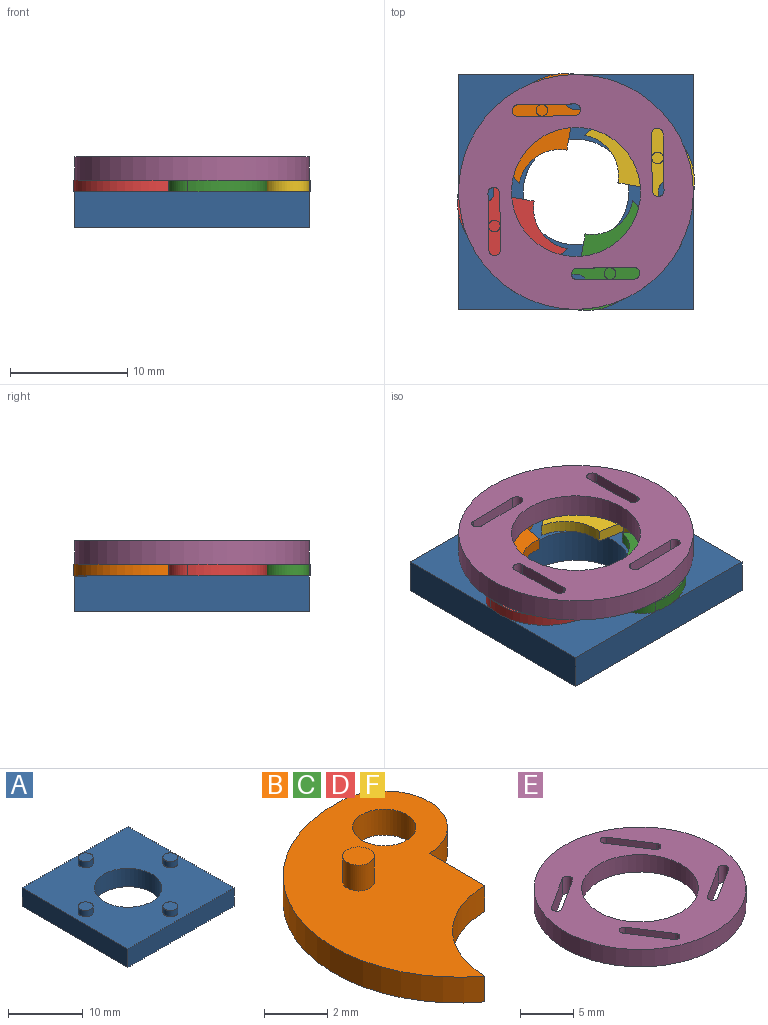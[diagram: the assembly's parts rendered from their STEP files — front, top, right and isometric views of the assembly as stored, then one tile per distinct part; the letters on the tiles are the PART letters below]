
ASSEMBLY  parts=6 mates=6
PART A: 15 faces, bbox 20x20x4 mm
  f0: plane 20x3mm, normal (1,0,0), area 60mm2, adj f1,f4,f5,f6
  f1: plane 20x3mm, normal (0,1,0), area 60mm2, adj f0,f2,f5,f6
  f2: plane 20x3mm, normal (-1,0,0), area 60mm2, adj f1,f4,f5,f6
  f3: cylinder r=4.5mm len=9mm, axis (0,0,-1), area 84.8mm2, adj f5,f6
  f4: plane 20x3mm, normal (0,-1,0), area 60mm2, adj f0,f2,f5,f6
  f5: plane 20x20mm, normal (0,0,1), area 323.8mm2, adj f0,f1,f2,f3,f4,f7,f9,f11
  f6: plane 20x20mm, normal (0,0,-1), area 336.4mm2, adj f0,f1,f2,f3,f4
  f7: cylinder r=1mm len=2mm, axis (0,0,-1), area 6.3mm2, adj f5,f8
  f8: plane 2x2mm, normal (0,0,1), area 3.1mm2, adj f7
  f9: cylinder r=1mm len=2mm, axis (0,0,-1), area 6.3mm2, adj f5,f10
  f10: plane 2x2mm, normal (0,0,1), area 3.1mm2, adj f9
  f11: cylinder r=1mm len=2mm, axis (0,0,-1), area 6.3mm2, adj f5,f12
  f12: plane 2x2mm, normal (0,0,1), area 3.1mm2, adj f11
  f13: cylinder r=1mm len=2mm, axis (0,0,-1), area 6.3mm2, adj f5,f14
  f14: plane 2x2mm, normal (0,0,1), area 3.1mm2, adj f13
PART B: 9 faces, bbox 7.8x10x2 mm
  f0: cylinder r=2mm len=4mm, axis (0,0,-1), area 6.3mm2, adj f1,f4,f5,f6
  f1: cylinder r=5.54mm len=10mm, axis (0,0,-1), area 14.1mm2, adj f0,f2,f5,f6
  f2: cylinder r=3.5mm len=3.5mm, axis (0,0,-1), area 5.5mm2, adj f1,f4,f5,f6
  f3: cylinder r=1mm len=2mm, axis (0,0,-1), area 6.3mm2, adj f5,f6
  f4: plane 2.5x1mm, normal (1,0,0), area 2.5mm2, adj f0,f2,f5,f6
  f5: plane 10x7.77mm, normal (0,0,1), area 40.8mm2, adj f0,f1,f2,f3,f4,f7
  f6: plane 10x7.77mm, normal (0,0,-1), area 41.6mm2, adj f0,f1,f2,f3,f4
  f7: cylinder r=0.5mm len=1mm, axis (0,0,-1), area 3.1mm2, adj f5,f8
  f8: plane 1x1mm, normal (0,0,1), area 0.8mm2, adj f7
PART C: same geometry as B
PART D: same geometry as B
PART E: 20 faces, bbox 20x20x2 mm
  f0: cylinder r=0.5mm len=2mm, axis (0,0,-1), area 3.1mm2, adj f1,f17,f18,f19
  f1: plane 4.05x2.62mm, normal (0.54,-0.84,0), area 9.6mm2, adj f0,f2,f18,f19
  f2: cylinder r=0.5mm len=2mm, axis (0,0,-1), area 3.1mm2, adj f1,f17,f18,f19
  f3: cylinder r=0.5mm len=2mm, axis (0,0,-1), area 3.1mm2, adj f4,f12,f18,f19
  f4: plane 4.05x2.62mm, normal (0.84,0.54,0), area 9.6mm2, adj f3,f5,f18,f19
  f5: cylinder r=0.5mm len=2mm, axis (0,0,-1), area 3.1mm2, adj f4,f12,f18,f19
  f6: cylinder r=0.5mm len=2mm, axis (0,0,-1), area 3.1mm2, adj f7,f13,f18,f19
  f7: plane 4.05x2.62mm, normal (-0.54,0.84,0), area 9.6mm2, adj f6,f8,f18,f19
  f8: cylinder r=0.5mm len=2mm, axis (0,0,-1), area 3.1mm2, adj f7,f13,f18,f19
  f9: cylinder r=0.5mm len=2mm, axis (0,0,-1), area 3.1mm2, adj f10,f14,f18,f19
  f10: plane 4.05x2.62mm, normal (-0.84,-0.54,0), area 9.6mm2, adj f9,f11,f18,f19
  f11: cylinder r=0.5mm len=2mm, axis (0,0,-1), area 3.1mm2, adj f10,f14,f18,f19
  f12: plane 4.05x2.62mm, normal (-0.84,-0.54,0), area 9.6mm2, adj f3,f5,f18,f19
  f13: plane 4.05x2.62mm, normal (0.54,-0.84,0), area 9.6mm2, adj f6,f8,f18,f19
  f14: plane 4.05x2.62mm, normal (0.84,0.54,0), area 9.6mm2, adj f9,f11,f18,f19
  f15: cylinder r=10mm len=20mm, axis (0,0,-1), area 125.7mm2, adj f18,f19
  f16: cylinder r=5.5mm len=11mm, axis (0,0,-1), area 69.1mm2, adj f18,f19
  f17: plane 4.05x2.62mm, normal (-0.54,0.84,0), area 9.6mm2, adj f0,f2,f18,f19
  f18: plane 20x20mm, normal (0,0,1), area 196.7mm2, adj f0,f1,f2,f3,f4,f5,f6,f7
  f19: plane 20x20mm, normal (0,0,-1), area 196.7mm2, adj f0,f1,f2,f3,f4,f5,f6,f7
PART F: same geometry as B
PLACE A t=(-29.83,-7.27,-2.84)mm fixed
PLACE B rot(axis=(0,0,-1),10deg) t=(-31.21,-7.15,0.16)mm
PLACE C rot(axis=(0,0,1),170deg) t=(-28.44,-7.39,0.16)mm
PLACE D rot(axis=(0,0,1),80deg) t=(-29.95,-8.66,0.16)mm
PLACE E rot(axis=(0,0,1),148deg) t=(-30.11,-9.94,1.16)mm
PLACE F rot(axis=(0,0,-1),100deg) t=(-29.7,-5.88,0.16)mm
MATE revolute B.f3 <-> A.f7  axis (0,0,1) through (-29.83,0.73,1.16)mm
MATE planar A.f7 <-> E.f15  axis (0,0,1) through (-29.83,0.73,1.16)mm
MATE cylindrical A.f3 <-> E.f15  axis (0,0,-1) through (-29.83,-7.27,-1.34)mm
MATE revolute C.f0 <-> A.f11  axis (0,0,1) through (-29.83,-15.27,1.16)mm
MATE revolute D.f0 <-> A.f9  axis (0,0,1) through (-37.83,-7.27,1.16)mm
MATE revolute F.f0 <-> A.f13  axis (0,0,1) through (-21.83,-7.27,1.16)mm
